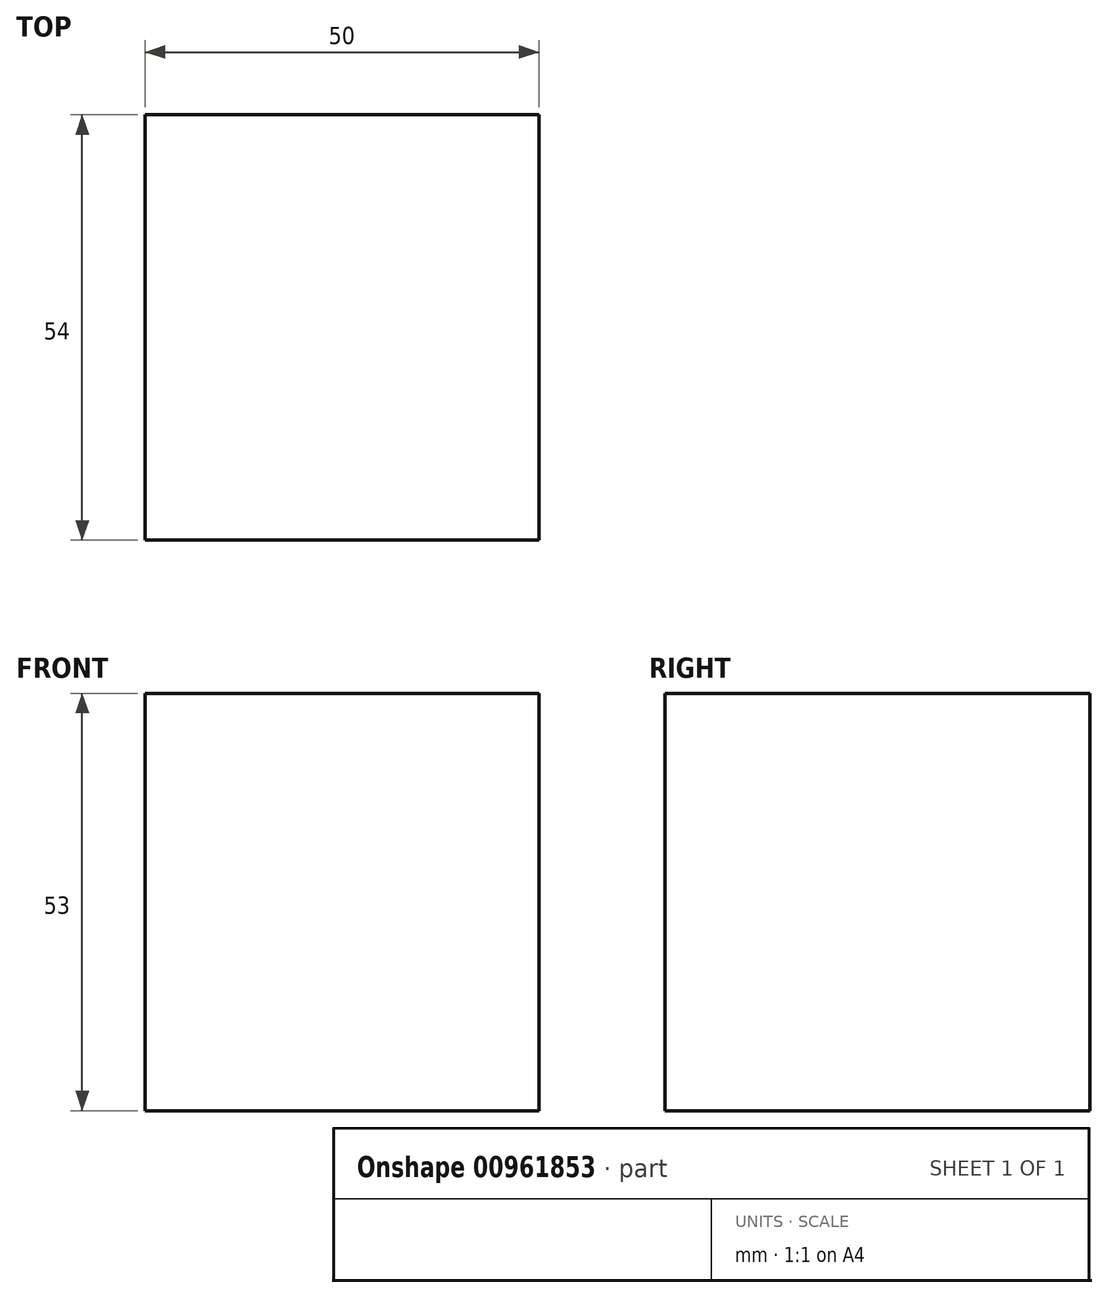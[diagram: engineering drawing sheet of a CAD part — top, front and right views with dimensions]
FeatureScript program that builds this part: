
annotation { "Feature Type Name" : "Feature", "Feature Type Description" : "" }
export const myFeature = defineFeature(function(context is Context, id is Id, definition is map)
    precondition{}
    {
        {
            var Q0;
            Q0=qCreatedBy(makeId("Top.planeOp"),FACE);
            var sketch = newSketch(context, id + "F0", { "sketchPlane" : qUnion([Q0])});
            skLineSegment(sketch, "E0.bottom", {"start": v(-40.43, 44.33) * mm, "end": v(9.57, 44.33) * mm});
            skLineSegment(sketch, "E0.top", {"start": v(-40.43, -9.67) * mm, "end": v(9.57, -9.67) * mm});
            skLineSegment(sketch, "E0.left", {"start": v(-40.43, 44.33) * mm, "end": v(-40.43, -9.67) * mm});
            skLineSegment(sketch, "E0.right", {"start": v(9.57, 44.33) * mm, "end": v(9.57, -9.67) * mm});
            skSolve(sketch);
        }
        {
            var Q0;
            Q0 = qSketchRegion(id + "F0", true);
            extrude(context, id + "F1", {"entities" : qUnion([Q0]), "depth" : 53 * mm, "offsetDistance" : 25 * mm});
        }
    });
